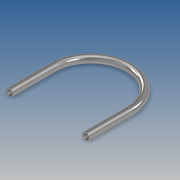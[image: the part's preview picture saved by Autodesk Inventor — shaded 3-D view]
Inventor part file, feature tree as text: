
AUTODESK INVENTOR PART (.ipt)
format: ipt  version: 2021.1 (Build 251245000, 245)  size: 134,144 bytes
history: native  units: mm
features: other x3, plane x1
ambient origin geometry x8: Origin, YZ Plane, XZ Plane, XY Plane, X Axis, Y Axis, Z Axis, Center Point
bodies: Solid1 (feature_tree)
feature tree (4):
  other  "Swing Bin Master - SB.ipt"
  other  "Upper Frame::Swing Bin Master - SB.ipt"
  other  "TaggingFeature1"
  plane  "Work Plane1"
